# Revit family: LR3322
name_source: partatom
category: Plumbing Fixtures
units: mm (PartAtom-declared; Revit-internal decimal feet)

## family parameters
Always vertical = Yes
Cut with Voids When Loaded = No
OmniClass Number = 23.45.05.14.14
OmniClass Title = Sinks/Lavatories
Part Type = Normal
Room Calculation Point = No
Round Connector Dimension = Use Diameter
Shared = No
Work Plane-Based = No

## types (6) — shared parameters
2D Hole 1 = No
2D Hole 2 = No
2D Hole 3 = No
2D Hole 4 = No
2D Hole 5 = No
Bowl Length = 1' - 1 1/2"
CL Sink to CL Partition = 0' - 0"
Custom Bowl = No
Custom Bowl Length = 1' - 1 1/2"
Description = Lustertone Double Bowl Sink
Drain Location = 0' - 8"
Faucet Hole CL = 0' - 1 3/4"
Hole 1 Top = 0' - 2 23/128"
Hole 1 to 2 = 0' - 4"
Hole 1 to 3 = 0' - 8"
Hole 1 to 4 = 1' - 0"
Installation Sheet URL = http://www.elkayusa.com
Left Bowl Length = 1' - 1 1/2"
Manufacturer = Elkay Manufacturing
Minimum Cabinet Width = 36"
Partition Width = 0' - 1 1/4"
Sink Bowl Formula = 1' - 1 1/2"
Sink Depth = 0' - 8 1/8"
Sink Ledge Back Width = 0' - 4 1/8"
Sink Ledge Front Width = 0' - 1 7/8"
Sink Ledge Sides Width = 0' - 2 3/8"
Sink Length = 2' - 9"
Sink Material = Metal - Steel - Stainless - Chrome
Sink Width = 1' - 10"
Specification Sheet URL = http://www.elkayusa.com
URL = www.elkayusa.com

## per-type parameters (varying)
| type | Hole 1 from CL | Hole 1 to 5 | Hole 2 Top | Hole 3 Top | Hole 4 Top | Hole 5 Top |
| LR33225 | 0' - 8" | 1' - 4" | 0' - 2 23/128" | 0' - 2 23/128" | 0' - 2 23/128" | 0' - 2 23/128" |
| LR33224 | 0' - 4" | 1' - 3" | 0' - 2 23/128" | 0' - 2 23/128" | 0' - 2 23/128" | 0' - 1 1/2" |
| LR33223 | 0' - 4" | 1' - 3" | 0' - 2 23/128" | 0' - 2 23/128" | 0' - 1 1/2" | 0' - 1 1/2" |
| LR3322MR2 | 0' - 0" | 1' - 3" | 0' - 2 23/128" | 0' - 1 1/2" | 0' - 1 1/2" | 0' - 1 1/2" |
| LR33222 | 0' - 2" | 1' - 3" | 0' - 2 23/128" | 0' - 1 1/2" | 0' - 1 1/2" | 0' - 1 1/2" |
| LR33221 | 0' - 0" | 1' - 3" | 0' - 1 1/2" | 0' - 1 1/2" | 0' - 1 1/2" | 0' - 1 1/2" |

note: column(s) folded — value = type name in every type: Model

## geometry (parser evidence)
native form markers: Blend x4, Sweep x6
no freeform markers — native parametric forms only
